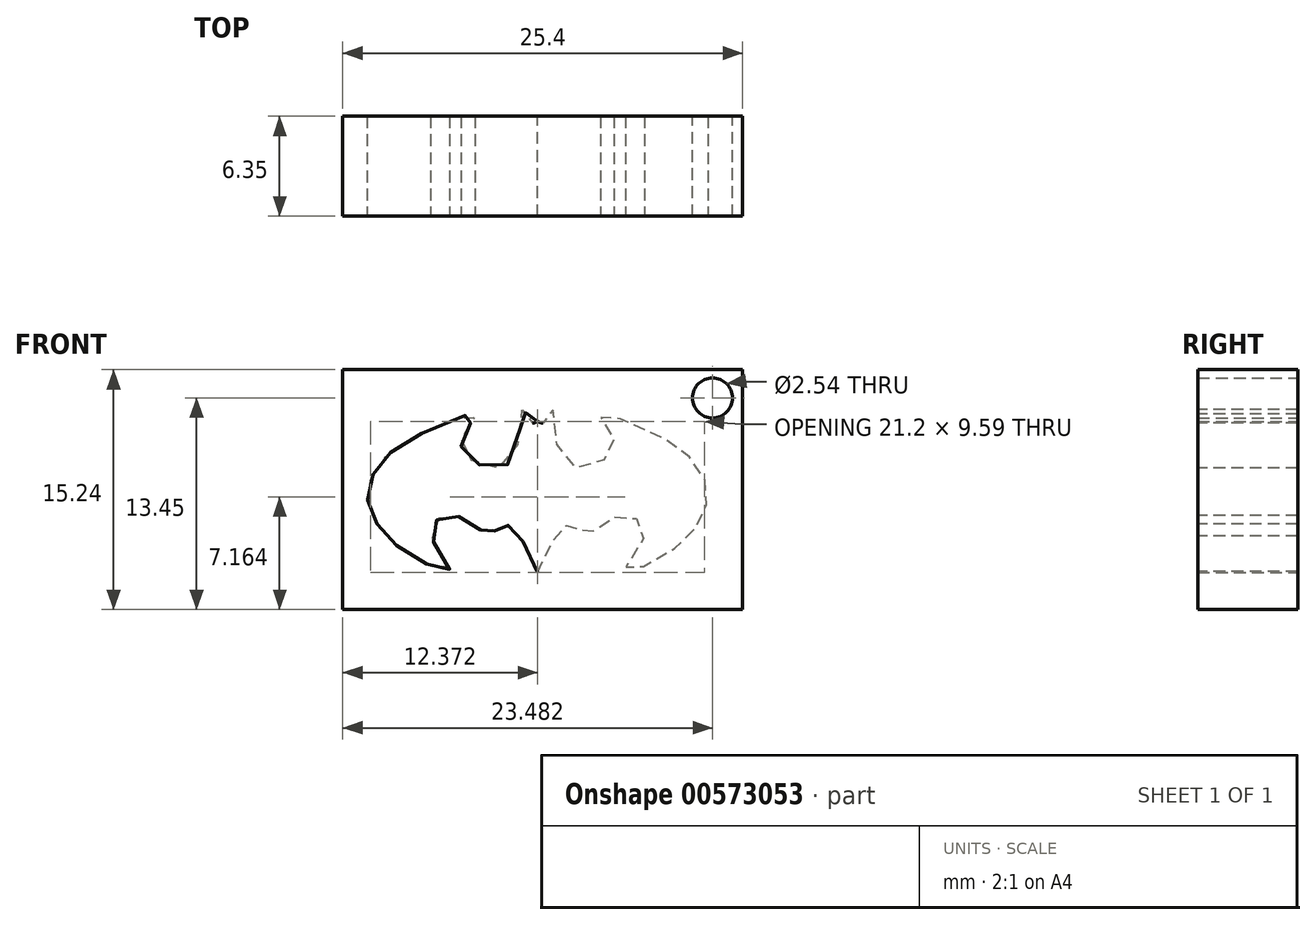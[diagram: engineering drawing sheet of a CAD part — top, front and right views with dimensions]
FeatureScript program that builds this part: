
annotation { "Feature Type Name" : "Feature", "Feature Type Description" : "" }
export const myFeature = defineFeature(function(context is Context, id is Id, definition is map)
    precondition{}
    {
        {
            var Q0;
            Q0=qCreatedBy(makeId("Front.planeOp"),FACE);
            var sketch = newSketch(context, id + "F0", { "sketchPlane" : qUnion([Q0])});
            skLineSegment(sketch, "E0", {"start": v(0, 0) * mm, "end": v(0, 15.24) * mm});
            skLineSegment(sketch, "E1", {"start": v(0, 0) * mm, "end": v(25.4, 0) * mm});
            skLineSegment(sketch, "E2", {"start": v(25.4, 0) * mm, "end": v(25.4, 15.24) * mm});
            skLineSegment(sketch, "E3", {"start": v(0, 15.24) * mm, "end": v(25.4, 15.24) * mm});
            skSolve(sketch);
        }
        {
            var Q0;
            Q0=makeQuery(id+"F0.imprint","IMPRINT",FACE,{"disambiguationData":[TD([[makeQuery(id+"F0.imprint","IMPRINT",EDGE,{"derivedFrom":sQuery(id+"F0.wireOp",EDGE,"E0")}),-1.0]])]});
            extrude(context, id + "F1", {"entities" : qUnion([Q0]), "depth" : 6.35 * mm, "offsetDistance" : 25.4 * mm});
        }
        {
            var Q0;
            Q0=qCreatedBy(makeId("Front.planeOp"),FACE);
            var sketch = newSketch(context, id + "F2", { "sketchPlane" : qUnion([Q0])});
            skLineSegment(sketch, "E4", {"start": v(12.37, 42.03) * mm, "end": v(12.37, 27.25) * mm});
            skFitSpline(sketch, "E5", {"points": [v(12.37, 2.37) * mm, v(13.53, 4.73) * mm, v(14.32, 5.4) * mm, v(14.89, 5.35) * mm, v(15.37, 4.69) * mm, v(16.16, 5.22) * mm, v(17.6, 5.96) * mm, v(18.79, 5.7) * mm, v(19.1, 4.51) * mm, v(17.95, 2.5) * mm, v(19.84, 3.11) * mm, v(21.98, 4.69) * mm, v(22.99, 6.22) * mm, v(23.12, 7.84) * mm, v(22.2, 9.5) * mm, v(19.97, 11.08) * mm, v(16.38, 12.4) * mm, v(16.95, 11.43) * mm, v(17.12, 10.08) * mm, v(15.5, 9.02) * mm, v(13.8, 9.81) * mm, v(13.31, 12.7) * mm, v(12.79, 11.91) * mm, v(12.37, 11.96) * mm], "startDerivative": vector(27.45, 47.85) * mm, "endDerivative": vector(-26.97, 11.8) * mm});
            skFitSpline(sketch, "E6.MirrorCS", {"points": [v(12.37, 2.37) * mm, v(11.21, 4.73) * mm, v(10.43, 5.4) * mm, v(9.86, 5.35) * mm, v(9.37, 4.69) * mm, v(8.59, 5.22) * mm, v(7.14, 5.96) * mm, v(5.96, 5.7) * mm, v(5.65, 4.51) * mm, v(6.8, 2.5) * mm, v(4.9, 3.11) * mm, v(2.76, 4.69) * mm, v(1.76, 6.22) * mm, v(1.62, 7.84) * mm, v(2.54, 9.5) * mm, v(4.78, 11.08) * mm, v(8.37, 12.4) * mm, v(7.8, 11.43) * mm, v(7.62, 10.08) * mm, v(9.24, 9.02) * mm, v(10.95, 9.81) * mm, v(11.43, 12.7) * mm, v(11.96, 11.91) * mm, v(12.37, 11.96) * mm], "startDerivative": vector(-27.45, 47.85) * mm, "endDerivative": vector(26.97, 11.8) * mm});
            skLineSegment(sketch, "E7", {"start": v(12.37, 2.37) * mm, "end": v(12.37, 11.96) * mm});
            skSolve(sketch);
        }
        {
            var Q0;
            Q0 = qSketchRegion(id + "F2", true);
            extrude(context, id + "F3", {"entities" : qUnion([Q0]), "operationType" : NewBodyOperationType.REMOVE, "depth" : 25.4 * mm, "offsetDistance" : 25.4 * mm});
        }
        {
            var Q0;
            Q0=qCreatedBy(makeId("Front.planeOp"),FACE);
            var sketch = newSketch(context, id + "F4", { "sketchPlane" : qUnion([Q0])});
            skCircle(sketch, "E8", {"center": v(23.48, 13.45) * mm, "radius": 1.27 * mm});
            skSolve(sketch);
        }
        {
            var Q0;
            Q0=makeQuery(id+"F4.imprint","IMPRINT",FACE,{"disambiguationData":[TD([[makeQuery(id+"F4.imprint","IMPRINT",EDGE,{"derivedFrom":sQuery(id+"F4.wireOp",EDGE,"E8")}),1.0]])]});
            extrude(context, id + "F5", {"entities" : qUnion([Q0]), "operationType" : NewBodyOperationType.REMOVE, "depth" : 25.4 * mm, "offsetDistance" : 25.4 * mm});
        }
    });
